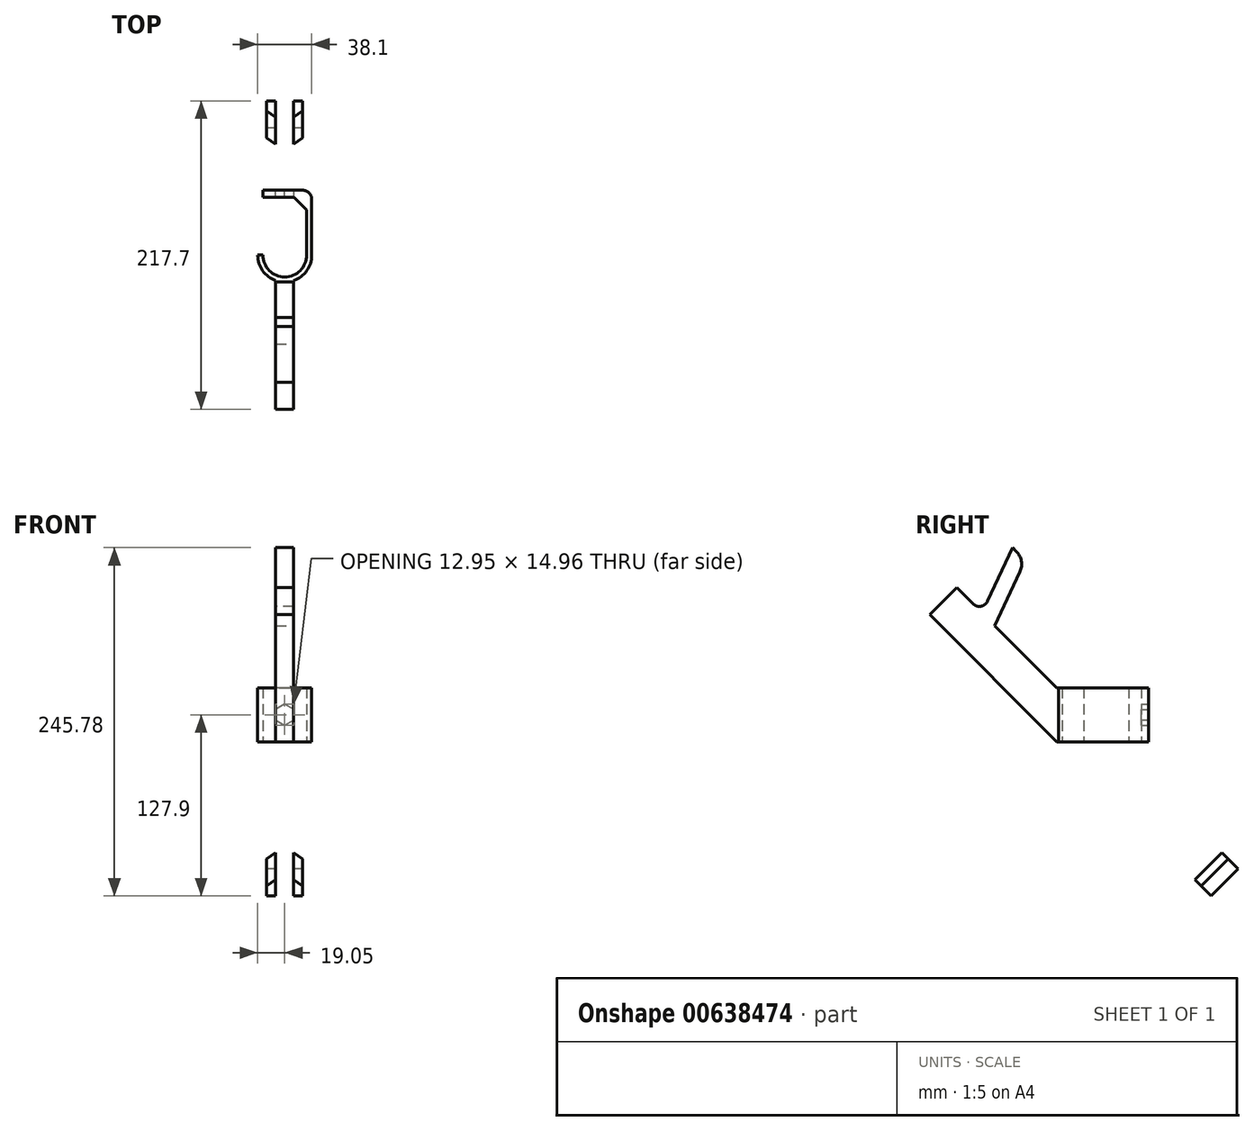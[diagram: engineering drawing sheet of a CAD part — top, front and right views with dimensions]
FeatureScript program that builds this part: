
annotation { "Feature Type Name" : "Feature", "Feature Type Description" : "" }
export const myFeature = defineFeature(function(context is Context, id is Id, definition is map)
    precondition{}
    {
        {
            var Q0;
            Q0=qCreatedBy(makeId("Top.planeOp"),FACE);
            var sketch = newSketch(context, id + "F0", { "sketchPlane" : qUnion([Q0])});
            skArc(sketch, "E0", {"start": v(-15.44, 0) * mm, "mid": v(0, -15.44) * mm, "end": v(15.44, 0) * mm});
            skArc(sketch, "E1", {"start": v(-19.05, 0) * mm, "mid": v(0, -19.05) * mm, "end": v(19.05, 0) * mm});
            skLineSegment(sketch, "E2", {"start": v(15.44, 0) * mm, "end": v(15.44, 34.3) * mm});
            skLineSegment(sketch, "E3", {"start": v(19.05, 0) * mm, "end": v(19.05, 44.45) * mm});
            skLineSegment(sketch, "E4", {"start": v(-15.44, 0) * mm, "end": v(-19.05, 0) * mm});
            skLineSegment(sketch, "E5", {"start": v(-19.05, 0) * mm, "end": v(-19.05, 2.54) * mm});
            skLineSegment(sketch, "E6", {"start": v(-19.05, 2.54) * mm, "end": v(-15.44, 2.54) * mm});
            skLineSegment(sketch, "E7", {"start": v(-15.44, 2.54) * mm, "end": v(-15.44, 0) * mm});
            skLineSegment(sketch, "E8", {"start": v(12.7, 45.72) * mm, "end": v(-15.44, 45.72) * mm});
            skLineSegment(sketch, "E9", {"start": v(-15.44, 45.72) * mm, "end": v(-15.44, 40.64) * mm});
            skLineSegment(sketch, "E10", {"start": v(-15.44, 40.64) * mm, "end": v(9.1, 40.64) * mm});
            skArc(sketch, "E11.filletArc", {"start": v(15.44, 34.3) * mm, "mid": v(13.58, 38.78) * mm, "end": v(9.1, 40.64) * mm});
            skPoint(sketch, "E12.visualSharp", {"position": v(19.05, 44.45) * mm});
            skLineSegment(sketch, "E13", {"start": v(15.44, 34.3) * mm, "end": v(15.44, 40.64) * mm});
            skLineSegment(sketch, "E14", {"start": v(15.44, 40.64) * mm, "end": v(9.1, 40.64) * mm});
            skLineSegment(sketch, "E15", {"start": v(6.55, 40.64) * mm, "end": v(15.44, 31.75) * mm});
            skLineSegment(sketch, "E16", {"start": v(19.05, 39.37) * mm, "end": v(19.05, 44.45) * mm});
            skPoint(sketch, "E17.visualSharp", {"position": v(19.05, 45.72) * mm});
            skArc(sketch, "E17.filletArc", {"start": v(19.05, 39.37) * mm, "mid": v(17.2, 43.86) * mm, "end": v(12.7, 45.72) * mm});
            skSolve(sketch);
        }
        {
            var Q0;
            Q0=makeQuery(id+"F0.imprint","IMPRINT",FACE,{"disambiguationData":[TD([[makeQuery(id+"F0.imprint","IMPRINT",EDGE,{"derivedFrom":sQuery(id+"F0.wireOp",EDGE,"E0")}),-1.0]])]});
            var Q1;
            {var subQ0=sQuery(id+"F0.wireOp",EDGE,"E11.filletArc");Q1=makeQuery(id+"F0.imprint","IMPRINT",FACE,{"disambiguationData":[TD([[makeQuery(id+"F0.imprint","IMPRINT",EDGE,{"derivedFrom":subQ0}),1.0]])]});}
            var Q2;
            Q2=makeQuery(id+"F0.imprint","IMPRINT",FACE,{"disambiguationData":[TD([[makeQuery(id+"F0.imprint","IMPRINT",EDGE,{"derivedFrom":sQuery(id+"F0.wireOp",EDGE,"E11.filletArc")}),-1.0]])]});
            extrude(context, id + "F1", {"entities" : qUnion([Q0, Q1, Q2]), "depth" : 38.1 * mm, "offsetDistance" : 25.4 * mm});
        }
        {
            var Q0;
            Q0=qCreatedBy(makeId("Right.planeOp"),FACE);
            var sketch = newSketch(context, id + "F2", { "sketchPlane" : qUnion([Q0])});
            skLineSegment(sketch, "E18", {"start": v(-19.05, 0) * mm, "end": v(-19.05, 38.1) * mm});
            skLineSegment(sketch, "E19", {"start": v(-19.05, 0) * mm, "end": v(-108.85, 89.8) * mm});
            skLineSegment(sketch, "E20", {"start": v(-19.05, 38.1) * mm, "end": v(-89.8, 108.85) * mm});
            skLineSegment(sketch, "E21", {"start": v(-108.85, 89.8) * mm, "end": v(-89.8, 108.85) * mm});
            skLineSegment(sketch, "E22.0.0", {"start": v(0, 38.1) * mm, "end": v(0, 38.1) * mm});
            skLineSegment(sketch, "E22.0.6", {"start": v(40.84, 38.1) * mm, "end": v(0, 38.1) * mm});
            skLineSegment(sketch, "E22.0.7", {"start": v(0, 38.1) * mm, "end": v(-15.44, 38.1) * mm});
            skLineSegment(sketch, "E22.0.9", {"start": v(0, 38.1) * mm, "end": v(-19.05, 38.1) * mm});
            skLineSegment(sketch, "E23", {"start": v(-15.44, 38.1) * mm, "end": v(-15.44, 0) * mm});
            skLineSegment(sketch, "E24", {"start": v(-15.44, 0) * mm, "end": v(-19.05, 0) * mm});
            skSolve(sketch);
        }
        {
            var Q0;
            Q0=makeQuery(id+"F2.imprint","IMPRINT",FACE,{"disambiguationData":[TD([[makeQuery(id+"F2.imprint","IMPRINT",EDGE,{"derivedFrom":sQuery(id+"F2.wireOp",EDGE,"E18")}),1.0]])]});
            var Q1;
            Q1=makeQuery(id+"F2.imprint","IMPRINT",FACE,{"disambiguationData":[TD([[makeQuery(id+"F2.imprint","IMPRINT",EDGE,{"derivedFrom":sQuery(id+"F2.wireOp",EDGE,"E18")}),-1.0]])]});
            extrude(context, id + "F3", {"entities" : qUnion([Q0, Q1]), "operationType" : NewBodyOperationType.ADD, "endBound" : BoundingType.SYMMETRIC, "depth" : 12.7 * mm, "offsetDistance" : 25.4 * mm});
        }
        {
            var Q0;
            Q0=makeQuery(id+"F3.opExtrude","CAP_FACE",FACE,{"disambiguationData":[OSD([sQuery(id+"F2.wireOp",EDGE,"E19"),sQuery(id+"F2.wireOp",EDGE,"E20"),sQuery(id+"F2.wireOp",EDGE,"E21"),sQuery(id+"F2.wireOp",EDGE,"qtFukV6V-MjEn-SjeW-6Dr2-Rb0Je2flICQ6"),sQuery(id+"F2.wireOp",EDGE,"bk9OrffV-8c4B-oz69-KPa2-X8SoJ85aSm0i"),sQuery(id+"F2.wireOp",EDGE,"DK7t6417-Z4kS-U3kZ-RFxf-M1bgH7PNUMAJ")])],"isStart":false});
            var sketch = newSketch(context, id + "F4", { "sketchPlane" : qUnion([Q0])});
            skLineSegment(sketch, "E25", {"start": v(-71.84, 90.9) * mm, "end": v(-50.37, 136.93) * mm});
            skLineSegment(sketch, "E26", {"start": v(-62.86, 81.91) * mm, "end": v(-41.4, 127.95) * mm});
            skLineSegment(sketch, "E27", {"start": v(-41.4, 127.95) * mm, "end": v(-50.37, 136.93) * mm});
            skSolve(sketch);
        }
        {
            var Q0;
            {var subQ0=sQuery(id+"F4.wireOp",EDGE,"E25");Q0=makeQuery(id+"F4.imprint","IMPRINT",FACE,{"disambiguationData":[TD([[makeQuery(id+"F4.imprint","IMPRINT",EDGE,{"derivedFrom":subQ0}),-1.0]])]});}
            var Q1;
            Q1=makeQuery(id+"F3.opExtrude","CAP_FACE",FACE,{"disambiguationData":[OSD([sQuery(id+"F2.wireOp",EDGE,"E19"),sQuery(id+"F2.wireOp",EDGE,"E20"),sQuery(id+"F2.wireOp",EDGE,"E21"),sQuery(id+"F2.wireOp",EDGE,"qtFukV6V-MjEn-SjeW-6Dr2-Rb0Je2flICQ6"),sQuery(id+"F2.wireOp",EDGE,"bk9OrffV-8c4B-oz69-KPa2-X8SoJ85aSm0i"),sQuery(id+"F2.wireOp",EDGE,"DK7t6417-Z4kS-U3kZ-RFxf-M1bgH7PNUMAJ")])],"isStart":true});
            extrude(context, id + "F5", {"entities" : qUnion([Q0]), "operationType" : NewBodyOperationType.ADD, "endBound" : BoundingType.UP_TO_SURFACE, "oppositeDirection" : true, "depth" : 25.4 * mm, "endBoundEntityFace" : qUnion([Q1]), "offsetDistance" : 25.4 * mm});
        }
        {
            var Q0;
            Q0=makeQuery(id+"F5.opExtrude","SWEPT_EDGE",EDGE,{"disambiguationData":[OSD([sQuery(id+"F2.wireOp",EDGE,"E20"),sQuery(id+"F4.wireOp",EDGE,"E25")])]});
            var Q1;
            Q1=makeQuery(id+"F5.opExtrude","SWEPT_EDGE",EDGE,{"disambiguationData":[OSD([sQuery(id+"F2.wireOp",EDGE,"E20"),sQuery(id+"F4.wireOp",EDGE,"E26")])]});
            fillet(context, id + "F6", {"entities" : qUnion([Q0, Q1]), "radius" : 6.35 * mm, "tangentPropagation" : true, "allowEdgeOverflow" : false});
        }
        {
            var Q0;
            Q0=makeQuery(id+"F5.opExtrude","SWEPT_EDGE",EDGE,{"disambiguationData":[OSD([sQuery(id+"F4.wireOp",EDGE,"E26"),sQuery(id+"F4.wireOp",EDGE,"E27")])]});
            fillet(context, id + "F7", {"entities" : qUnion([Q0]), "radius" : 12.7 * mm, "tangentPropagation" : true, "allowEdgeOverflow" : false});
        }
        {
            var Q0;
            {var subQ3=sQuery(id+"F2.wireOp",EDGE,"E21");var subQ4=sQuery(id+"F2.wireOp",EDGE,"E20");Q0=makeQuery(id+"F5.boolean.opBoolean","SPLIT",FACE,{"disambiguationData":[TD([makeQuery(id+"F3.opExtrude","SWEPT_FACE",FACE,{"disambiguationData":[OSD([subQ3])]})])],"derivedFrom":makeQuery(id+"F3.opExtrude","SWEPT_FACE",FACE,{"disambiguationData":[OSD([subQ4])]})});}
            var sketch = newSketch(context, id + "F8", { "sketchPlane" : qUnion([Q0])});
            skLineSegment(sketch, "E28.0.0", {"start": v(6.35, -140.47) * mm, "end": v(6.35, -124.14) * mm});
            skLineSegment(sketch, "E28.0.1", {"start": v(6.35, -124.14) * mm, "end": v(-6.35, -124.14) * mm});
            skLineSegment(sketch, "E28.0.2", {"start": v(-6.35, -124.14) * mm, "end": v(-6.35, -140.47) * mm});
            skLineSegment(sketch, "E28.0.3", {"start": v(-6.35, -140.47) * mm, "end": v(6.35, -140.47) * mm});
            skLineSegment(sketch, "E29", {"start": v(-12.7, -140.47) * mm, "end": v(12.7, -140.47) * mm});
            skLineSegment(sketch, "E30", {"start": v(-12.7, -140.47) * mm, "end": v(-12.7, -130.31) * mm});
            skLineSegment(sketch, "E31", {"start": v(-12.7, -130.31) * mm, "end": v(12.7, -130.31) * mm});
            skLineSegment(sketch, "E32", {"start": v(12.7, -130.31) * mm, "end": v(12.7, -140.47) * mm});
            skLineSegment(sketch, "E33", {"start": v(-12.7, -130.31) * mm, "end": v(-6.35, -124.14) * mm});
            skLineSegment(sketch, "E34", {"start": v(12.7, -130.31) * mm, "end": v(6.35, -124.14) * mm});
            skSolve(sketch);
        }
        {
            var Q0;
            {var subQ0=sQuery(id+"F8.wireOp",EDGE,"hoZSziUU-nJGk-sYhJ-dFJN-nhbxAgzul4YK");Q0=makeQuery(id+"F8.imprint","IMPRINT",FACE,{"disambiguationData":[TD([[makeQuery(id+"F8.imprint","IMPRINT",EDGE,{"derivedFrom":subQ0}),1.0]])]});}
            var Q1;
            {var subQ0=sQuery(id+"F8.wireOp",EDGE,"E30");Q1=makeQuery(id+"F8.imprint","IMPRINT",FACE,{"disambiguationData":[TD([[makeQuery(id+"F8.imprint","IMPRINT",EDGE,{"derivedFrom":subQ0}),-1.0]])]});}
            var Q2;
            {var subQ0=sQuery(id+"F8.wireOp",EDGE,"E32");Q2=makeQuery(id+"F8.imprint","IMPRINT",FACE,{"disambiguationData":[TD([[makeQuery(id+"F8.imprint","IMPRINT",EDGE,{"derivedFrom":subQ0}),-1.0]])]});}
            var Q3;
            {var subQ5=sQuery(id+"F8.wireOp",EDGE,"4bovK6SA-rUkF-shkB-RS3m-2b03cJL1w4Gw");Q3=makeQuery(id+"F8.imprint","IMPRINT",FACE,{"disambiguationData":[TD([[makeQuery(id+"F8.imprint","IMPRINT",EDGE,{"derivedFrom":subQ5}),1.0]])]});}
            var Q4;
            {var subQ0=sQuery(id+"F8.wireOp",EDGE,"E33");Q4=makeQuery(id+"F8.imprint","IMPRINT",FACE,{"disambiguationData":[TD([[makeQuery(id+"F8.imprint","IMPRINT",EDGE,{"derivedFrom":subQ0}),-1.0]])]});}
            var Q5;
            {var subQ0=sQuery(id+"F8.wireOp",EDGE,"E34");Q5=makeQuery(id+"F8.imprint","IMPRINT",FACE,{"disambiguationData":[TD([[makeQuery(id+"F8.imprint","IMPRINT",EDGE,{"derivedFrom":subQ0}),1.0]])]});}
            var Q6;
            Q6=makeQuery(id+"F3.opExtrude","SWEPT_FACE",FACE,{"disambiguationData":[OSD([sQuery(id+"F2.wireOp",EDGE,"E19")])]});
            extrude(context, id + "F9", {"entities" : qUnion([Q0, Q1, Q2, Q3, Q4, Q5]), "operationType" : NewBodyOperationType.ADD, "endBound" : BoundingType.UP_TO_SURFACE, "oppositeDirection" : true, "depth" : 25.4 * mm, "endBoundEntityFace" : qUnion([Q6]), "offsetDistance" : 25.4 * mm});
        }
        {
            var Q0;
            {var subQ0=sQuery(id+"F8.wireOp",EDGE,"E31");var subQ1=sQuery(id+"F8.wireOp",EDGE,"E29");var subQ5=sQuery(id+"F2.wireOp",EDGE,"E21");var subQ6=sQuery(id+"F2.wireOp",EDGE,"E20");Q0=makeQuery(id+"F9.boolean.opBoolean","MERGE",FACE,{"derivedFrom":[makeQuery(id+"F5.boolean.opBoolean","SPLIT",FACE,{"disambiguationData":[TD([makeQuery(id+"F3.opExtrude","SWEPT_FACE",FACE,{"disambiguationData":[OSD([subQ5])]})])],"derivedFrom":makeQuery(id+"F3.opExtrude","SWEPT_FACE",FACE,{"disambiguationData":[OSD([subQ6])]})}),makeQuery(id+"F9.opExtrude","CAP_FACE",FACE,{"disambiguationData":[OSD([sQuery(id+"F8.wireOp",EDGE,"E28.0.0"),subQ1,subQ0,sQuery(id+"F8.wireOp",EDGE,"E32"),sQuery(id+"F8.wireOp",EDGE,"4bovK6SA-rUkF-shkB-RS3m-2b03cJL1w4Gw")])],"isStart":true}),makeQuery(id+"F9.opExtrude","CAP_FACE",FACE,{"disambiguationData":[OSD([sQuery(id+"F8.wireOp",EDGE,"E28.0.2"),subQ1,sQuery(id+"F8.wireOp",EDGE,"E30"),subQ0,sQuery(id+"F8.wireOp",EDGE,"1iqTP1gQ-9Ady-N5Ra-a7oZ-EJfbPKOUT4gc")])],"isStart":true})]});}
            var sketch = newSketch(context, id + "F10", { "sketchPlane" : qUnion([Q0])});
            skLineSegment(sketch, "E35.0.0", {"start": v(-12.7, -140.47) * mm, "end": v(12.7, -140.47) * mm});
            skLineSegment(sketch, "E35.0.1", {"start": v(12.7, -140.47) * mm, "end": v(12.7, -130.31) * mm});
            skLineSegment(sketch, "E35.0.4", {"start": v(6.35, -124.14) * mm, "end": v(-6.35, -124.14) * mm});
            skLineSegment(sketch, "E35.0.6", {"start": v(-12.52, -130.31) * mm, "end": v(-12.7, -130.31) * mm});
            skLineSegment(sketch, "E35.0.7", {"start": v(-12.7, -130.31) * mm, "end": v(-12.7, -140.47) * mm});
            skLineSegment(sketch, "E36", {"start": v(-6.35, -130.31) * mm, "end": v(6.35, -130.31) * mm});
            skLineSegment(sketch, "E37", {"start": v(6.35, -130.31) * mm, "end": v(3.81, -140.47) * mm});
            skLineSegment(sketch, "E38", {"start": v(-6.35, -130.31) * mm, "end": v(-3.8, -140.47) * mm});
            skLineSegment(sketch, "E39", {"start": v(0, -130.31) * mm, "end": v(0, -140.47) * mm});
            skLineSegment(sketch, "E40", {"start": v(-12.7, -130.31) * mm, "end": v(-6.35, -124.14) * mm});
            skLineSegment(sketch, "E41", {"start": v(6.35, -124.14) * mm, "end": v(12.7, -130.31) * mm});
            skSolve(sketch);
        }
        {
            var Q0;
            {var subQ0=sQuery(id+"F10.wireOp",EDGE,"E38");Q0=makeQuery(id+"F10.imprint","IMPRINT",FACE,{"disambiguationData":[TD([[makeQuery(id+"F10.imprint","IMPRINT",EDGE,{"derivedFrom":subQ0}),1.0]])]});}
            var Q1;
            {var subQ0=sQuery(id+"F10.wireOp",EDGE,"E37");Q1=makeQuery(id+"F10.imprint","IMPRINT",FACE,{"disambiguationData":[TD([[makeQuery(id+"F10.imprint","IMPRINT",EDGE,{"derivedFrom":subQ0}),-1.0]])]});}
            extrude(context, id + "F11", {"entities" : qUnion([Q0, Q1]), "operationType" : NewBodyOperationType.REMOVE, "oppositeDirection" : true, "depth" : 17.78 * mm, "offsetDistance" : 25.4 * mm});
        }
        {
            var Q0;
            Q0=makeQuery(id+"F1.opExtrude","SWEPT_FACE",FACE,{"disambiguationData":[OSD([sQuery(id+"F0.wireOp",EDGE,"E8")])]});
            var sketch = newSketch(context, id + "F12", { "sketchPlane" : qUnion([Q0])});
            skLineSegment(sketch, "E42.0.1", {"start": v(6.35, 0) * mm, "end": v(-6.35, 0) * mm});
            skLineSegment(sketch, "E43.0.0", {"start": v(-12.7, 0) * mm, "end": v(15.44, 0) * mm});
            skLineSegment(sketch, "E43.0.1", {"start": v(15.44, 0) * mm, "end": v(15.44, 38.1) * mm});
            skLineSegment(sketch, "E43.0.2", {"start": v(15.44, 38.1) * mm, "end": v(-12.7, 38.1) * mm});
            skLineSegment(sketch, "E43.0.3", {"start": v(-12.7, 38.1) * mm, "end": v(-12.7, 0) * mm});
            skLineSegment(sketch, "E44", {"start": v(-12.7, 19.05) * mm, "end": v(15.44, 19.05) * mm});
            skLineSegment(sketch, "E45", {"start": v(0, 0) * mm, "end": v(0, 38.1) * mm});
            skPoint(sketch, "E46.0.midPoint", {"position": v(6.35, 19.05) * mm});
            skCircle(sketch, "E47", {"center": v(0, 19.05) * mm, "radius": 6.48 * mm});
            skCircle(sketch, "E48.cCircle", {"center": v(0, 19.05) * mm, "radius": 6.48 * mm, "construction": true});
            skLineSegment(sketch, "E48.0", {"start": v(6.48, 22.79) * mm, "end": v(6.48, 15.31) * mm});
            skLineSegment(sketch, "E48.1", {"start": v(6.48, 15.31) * mm, "end": v(0, 11.57) * mm});
            skLineSegment(sketch, "E48.2", {"start": v(0, 11.57) * mm, "end": v(-6.48, 15.31) * mm});
            skLineSegment(sketch, "E48.3", {"start": v(-6.48, 15.31) * mm, "end": v(-6.48, 22.79) * mm});
            skLineSegment(sketch, "E48.4", {"start": v(-6.48, 22.79) * mm, "end": v(0, 26.53) * mm});
            skLineSegment(sketch, "E48.5", {"start": v(0, 26.53) * mm, "end": v(6.48, 22.79) * mm});
            skPoint(sketch, "E48.0.midPoint", {"position": v(6.48, 19.05) * mm});
            skSolve(sketch);
        }
        {
            var Q0;
            {var subQ0=sQuery(id+"F12.wireOp",EDGE,"E48.2");var subQ3=sQuery(id+"F12.wireOp",EDGE,"E48.3");var subQ5=makeQuery(id+"F12.imprint","INTERSECT",VERTEX,{"derivedFrom":[subQ0,subQ3]});Q0=makeQuery(id+"F12.imprint","IMPRINT",FACE,{"disambiguationData":[TD([[makeQuery(id+"F12.imprint","IMPRINT",EDGE,{"disambiguationData":[TD([[subQ5,1.0]])],"derivedFrom":subQ0}),-1.0]])]});}
            var Q1;
            {var subQ1=sQuery(id+"F12.wireOp",EDGE,"E45");var subQ3=sQuery(id+"F12.wireOp",EDGE,"E47");var subQ4=makeQuery(id+"F12.imprint","INTERSECT",VERTEX,{"disambiguationData":[OD(0.0)],"derivedFrom":[subQ1,subQ3]});Q1=makeQuery(id+"F12.imprint","IMPRINT",FACE,{"disambiguationData":[TD([[makeQuery(id+"F12.imprint","IMPRINT",EDGE,{"disambiguationData":[TD([[subQ4,1.0]])],"derivedFrom":subQ3}),-1.0]])]});}
            var Q2;
            {var subQ1=sQuery(id+"F12.wireOp",EDGE,"E45");var subQ3=sQuery(id+"F12.wireOp",EDGE,"E47");var subQ4=makeQuery(id+"F12.imprint","INTERSECT",VERTEX,{"disambiguationData":[OD(0.0)],"derivedFrom":[subQ1,subQ3]});Q2=makeQuery(id+"F12.imprint","IMPRINT",FACE,{"disambiguationData":[TD([[makeQuery(id+"F12.imprint","IMPRINT",EDGE,{"disambiguationData":[TD([[subQ4,-1.0]])],"derivedFrom":subQ3}),-1.0]])]});}
            var Q3;
            {var subQ0=sQuery(id+"F12.wireOp",EDGE,"E48.1");var subQ3=sQuery(id+"F12.wireOp",EDGE,"E48.0");var subQ5=makeQuery(id+"F12.imprint","INTERSECT",VERTEX,{"derivedFrom":[subQ3,subQ0]});Q3=makeQuery(id+"F12.imprint","IMPRINT",FACE,{"disambiguationData":[TD([[makeQuery(id+"F12.imprint","IMPRINT",EDGE,{"disambiguationData":[TD([[subQ5,-1.0]])],"derivedFrom":subQ0}),-1.0]])]});}
            var Q4;
            {var subQ0=sQuery(id+"F12.wireOp",EDGE,"E48.5");var subQ3=sQuery(id+"F12.wireOp",EDGE,"E48.0");var subQ5=makeQuery(id+"F12.imprint","INTERSECT",VERTEX,{"derivedFrom":[subQ3,subQ0]});Q4=makeQuery(id+"F12.imprint","IMPRINT",FACE,{"disambiguationData":[TD([[makeQuery(id+"F12.imprint","IMPRINT",EDGE,{"disambiguationData":[TD([[subQ5,1.0]])],"derivedFrom":subQ0}),-1.0]])]});}
            var Q5;
            {var subQ0=sQuery(id+"F12.wireOp",EDGE,"E48.4");var subQ3=sQuery(id+"F12.wireOp",EDGE,"E48.3");var subQ5=makeQuery(id+"F12.imprint","INTERSECT",VERTEX,{"derivedFrom":[subQ3,subQ0]});Q5=makeQuery(id+"F12.imprint","IMPRINT",FACE,{"disambiguationData":[TD([[makeQuery(id+"F12.imprint","IMPRINT",EDGE,{"disambiguationData":[TD([[subQ5,-1.0]])],"derivedFrom":subQ0}),-1.0]])]});}
            var Q6;
            {var subQ1=sQuery(id+"F12.wireOp",EDGE,"E45");var subQ3=sQuery(id+"F12.wireOp",EDGE,"E47");var subQ4=makeQuery(id+"F12.imprint","INTERSECT",VERTEX,{"disambiguationData":[OD(1.0)],"derivedFrom":[subQ1,subQ3]});Q6=makeQuery(id+"F12.imprint","IMPRINT",FACE,{"disambiguationData":[TD([[makeQuery(id+"F12.imprint","IMPRINT",EDGE,{"disambiguationData":[TD([[subQ4,-1.0]])],"derivedFrom":subQ3}),-1.0]])]});}
            var Q7;
            {var subQ1=sQuery(id+"F12.wireOp",EDGE,"E45");var subQ3=sQuery(id+"F12.wireOp",EDGE,"E47");var subQ4=makeQuery(id+"F12.imprint","INTERSECT",VERTEX,{"disambiguationData":[OD(1.0)],"derivedFrom":[subQ1,subQ3]});Q7=makeQuery(id+"F12.imprint","IMPRINT",FACE,{"disambiguationData":[TD([[makeQuery(id+"F12.imprint","IMPRINT",EDGE,{"disambiguationData":[TD([[subQ4,1.0]])],"derivedFrom":subQ3}),-1.0]])]});}
            var Q8;
            {var subQ0=sQuery(id+"F12.wireOp",EDGE,"E45");var subQ1=sQuery(id+"F12.wireOp",EDGE,"E44");var subQ2=makeQuery(id+"F12.imprint","INTERSECT",VERTEX,{"derivedFrom":[subQ1,subQ0]});Q8=makeQuery(id+"F12.imprint","IMPRINT",FACE,{"disambiguationData":[TD([[makeQuery(id+"F12.imprint","IMPRINT",EDGE,{"disambiguationData":[TD([[subQ2,-1.0]])],"derivedFrom":subQ0}),-1.0]])]});}
            var Q9;
            {var subQ0=sQuery(id+"F12.wireOp",EDGE,"E45");var subQ1=sQuery(id+"F12.wireOp",EDGE,"E44");var subQ2=makeQuery(id+"F12.imprint","INTERSECT",VERTEX,{"derivedFrom":[subQ1,subQ0]});Q9=makeQuery(id+"F12.imprint","IMPRINT",FACE,{"disambiguationData":[TD([[makeQuery(id+"F12.imprint","IMPRINT",EDGE,{"disambiguationData":[TD([[subQ2,-1.0]])],"derivedFrom":subQ0}),1.0]])]});}
            var Q10;
            {var subQ0=sQuery(id+"F12.wireOp",EDGE,"E45");var subQ1=sQuery(id+"F12.wireOp",EDGE,"E44");var subQ2=makeQuery(id+"F12.imprint","INTERSECT",VERTEX,{"derivedFrom":[subQ1,subQ0]});Q10=makeQuery(id+"F12.imprint","IMPRINT",FACE,{"disambiguationData":[TD([[makeQuery(id+"F12.imprint","IMPRINT",EDGE,{"disambiguationData":[TD([[subQ2,1.0]])],"derivedFrom":subQ0}),1.0]])]});}
            var Q11;
            {var subQ0=sQuery(id+"F12.wireOp",EDGE,"E45");var subQ1=sQuery(id+"F12.wireOp",EDGE,"E44");var subQ2=makeQuery(id+"F12.imprint","INTERSECT",VERTEX,{"derivedFrom":[subQ1,subQ0]});Q11=makeQuery(id+"F12.imprint","IMPRINT",FACE,{"disambiguationData":[TD([[makeQuery(id+"F12.imprint","IMPRINT",EDGE,{"disambiguationData":[TD([[subQ2,1.0]])],"derivedFrom":subQ0}),-1.0]])]});}
            extrude(context, id + "F13", {"entities" : qUnion([Q0, Q1, Q2, Q3, Q4, Q5, Q6, Q7, Q8, Q9, Q10, Q11]), "operationType" : NewBodyOperationType.REMOVE, "oppositeDirection" : true, "depth" : 25.4 * mm, "offsetDistance" : 25.4 * mm});
        }
    });
